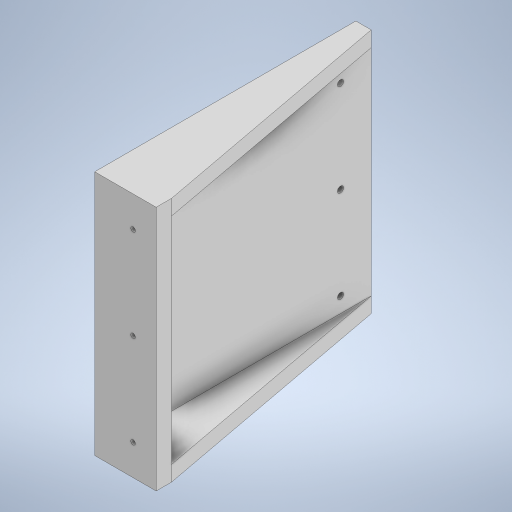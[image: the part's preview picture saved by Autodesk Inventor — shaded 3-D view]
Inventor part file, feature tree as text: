
AUTODESK INVENTOR PART (.ipt)
format: ipt  version: 2023 (Build 270158000, 158)  size: 317,952 bytes
history: native  units: mm
features: extrude x6, sketch x6
ambient origin geometry x8: Origin, YZ Plane, XZ Plane, XY Plane, X Axis, Y Axis, Z Axis, Center Point
bodies: Body1 (feature_tree)
feature tree (12):
  extrude  "Extrusion15"  Depth=160.0mm
  extrude  "Extrusion16"  Depth=170.0mm
  extrude  "Extrusion17"  Depth=10.0mm TaperAngle=0.0deg
  extrude  "Extrusion18"  Depth=10.0mm TaperAngle=0.0deg
  extrude  "Extrusion19"  Depth=3.0mm
  extrude  "Extrusion20"  Depth=20.0mm TaperAngle=0.0deg
  sketch  "Sketch21"  dims[d53=30.0mm d1=160.0mm]
  sketch  "Sketch22"  dims[d55=10.0mm d56=0.0mm d57=170.0mm]
  sketch  "Sketch23"  dims[d58=160.0mm d59=10.0mm d60=0.0mm]
  sketch  "Sketch24"  dims[d61=10.0mm d62=0.0mm d63=10.0mm d64=0.0mm]
  sketch  "Sketch25"  dims[d65=3.0mm d66=3.0mm]
  sketch  "Sketch27"  dims[d67=3.0mm d68=20.0mm d69=0.0mm d70=20.0mm d71=20.0mm d72=80.0mm d73=20.0mm d74=4.0mm d75=4.0mm d76=80.0mm d77=4.0mm d78=20.0mm d79=20.0mm d80=20.0mm d81=20.0mm d82=20.0mm d83=0.0mm d84=4.0mm d85=20.0mm d86=80.0mm d87=4.0mm d88=20.0mm d89=20.0mm d90=4.0mm d91=20.0mm d92=20.0mm d49=0.5mm d50=0.872665mm d51=0.5mm d52=0.872665mm]
